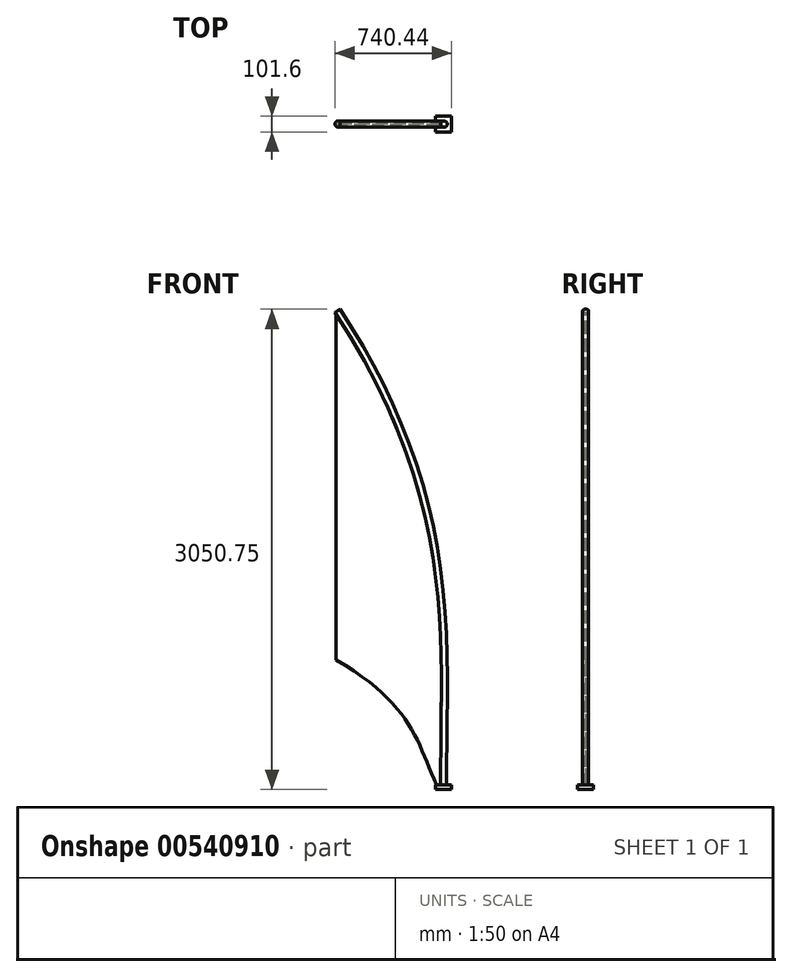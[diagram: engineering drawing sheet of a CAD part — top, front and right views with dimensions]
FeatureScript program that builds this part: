
annotation { "Feature Type Name" : "Feature", "Feature Type Description" : "" }
export const myFeature = defineFeature(function(context is Context, id is Id, definition is map)
    precondition{}
    {
        {
            var Q0;
            Q0=qCreatedBy(makeId("Front.planeOp"),FACE);
            var sketch = newSketch(context, id + "F0", { "sketchPlane" : qUnion([Q0])});
            skPoint(sketch, "E0", {"position": v(0, 2209.8) * mm});
            skPoint(sketch, "E1", {"position": v(671.64, -795.83) * mm});
            skPoint(sketch, "E2", {"position": v(639.8, -795.83) * mm});
            skLineSegment(sketch, "E3", {"start": v(639.8, -795.83) * mm, "end": v(671.64, -795.83) * mm});
            skLineSegment(sketch, "E4", {"start": v(0, 0) * mm, "end": v(0, 2209.8) * mm});
            skFitSpline(sketch, "E5", {"points": [v(0, 2209.8) * mm, v(671.64, -795.83) * mm], "startDerivative": vector(2383.4, -3651.75) * mm, "endDerivative": vector(17.92, -2687.25) * mm});
            skFitSpline(sketch, "E6", {"points": [v(0, 0) * mm, v(639.8, -795.83) * mm], "startDerivative": vector(1436.23, -844.66) * mm, "endDerivative": vector(391.6, -879.1) * mm});
            skSolve(sketch);
        }
        {
            var Q0;
            Q0 = qSketchRegion(id + "F0", true);
            extrude(context, id + "F1", {"entities" : qUnion([Q0]), "depth" : 2.54 * mm, "offsetDistance" : 25.4 * mm});
        }
        {
            var Q0;
            Q0=makeQuery(id+"F1.opExtrude","SWEPT_FACE",FACE,{"disambiguationData":[OSD([sQuery(id+"F0.wireOp",EDGE,"E3")])]});
            var sketch = newSketch(context, id + "F2", { "sketchPlane" : qUnion([Q0])});
            skLineSegment(sketch, "E7", {"start": v(671.64, 1.27) * mm, "end": v(684.34, 1.27) * mm, "construction": true});
            skCircle(sketch, "E8", {"center": v(684.34, 1.27) * mm, "radius": 19.05 * mm});
            skSolve(sketch);
        }
        {
            var Q0;
            {var subQ1=sQuery(id+"F0.wireOp",EDGE,"E3");var subQ6=makeQuery(id+"F1.opExtrude","SWEPT_EDGE",EDGE,{"disambiguationData":[OSD([subQ1,sQuery(id+"F0.wireOp",EDGE,"E5")])]});Q0=makeQuery(id+"F2.imprint","IMPRINT",FACE,{"disambiguationData":[TD([[makeQuery(id+"F2.imprint","IMPRINT",EDGE,{"derivedFrom":subQ6}),1.0]])]});}
            var Q1;
            Q1=makeQuery(id+"F1.opExtrude","CAP_EDGE",EDGE,{"disambiguationData":[OSD([sQuery(id+"F0.wireOp",EDGE,"E5")])],"isStart":false});
            sweep(context, id + "F3", {"profiles" : qUnion([Q0]), "path" : qUnion([Q1])});
        }
        {
            var Q0;
            Q0=makeQuery(id+"F3.opSweep","CAP_FACE",FACE,{"disambiguationData":[OSD([sQuery(id+"F0.wireOp",EDGE,"E3"),sQuery(id+"F0.wireOp",EDGE,"E5"),sQuery(id+"F2.wireOp",EDGE,"E8")])],"isStart":true});
            var sketch = newSketch(context, id + "F4", { "sketchPlane" : qUnion([Q0])});
            skLineSegment(sketch, "E9.bottom", {"start": v(633.54, 52.07) * mm, "end": v(735.14, 52.07) * mm});
            skLineSegment(sketch, "E9.top", {"start": v(633.54, -49.53) * mm, "end": v(735.14, -49.53) * mm});
            skLineSegment(sketch, "E9.left", {"start": v(633.54, 52.07) * mm, "end": v(633.54, -49.53) * mm});
            skLineSegment(sketch, "E9.right", {"start": v(735.14, 52.07) * mm, "end": v(735.14, -49.53) * mm});
            skPoint(sketch, "E9.middle", {"position": v(684.34, 1.27) * mm});
            skSolve(sketch);
        }
        {
            var Q0;
            Q0 = qSketchRegion(id + "F4", true);
            extrude(context, id + "F5", {"entities" : qUnion([Q0]), "depth" : 27.94 * mm, "offsetDistance" : 25.4 * mm});
        }
    });
